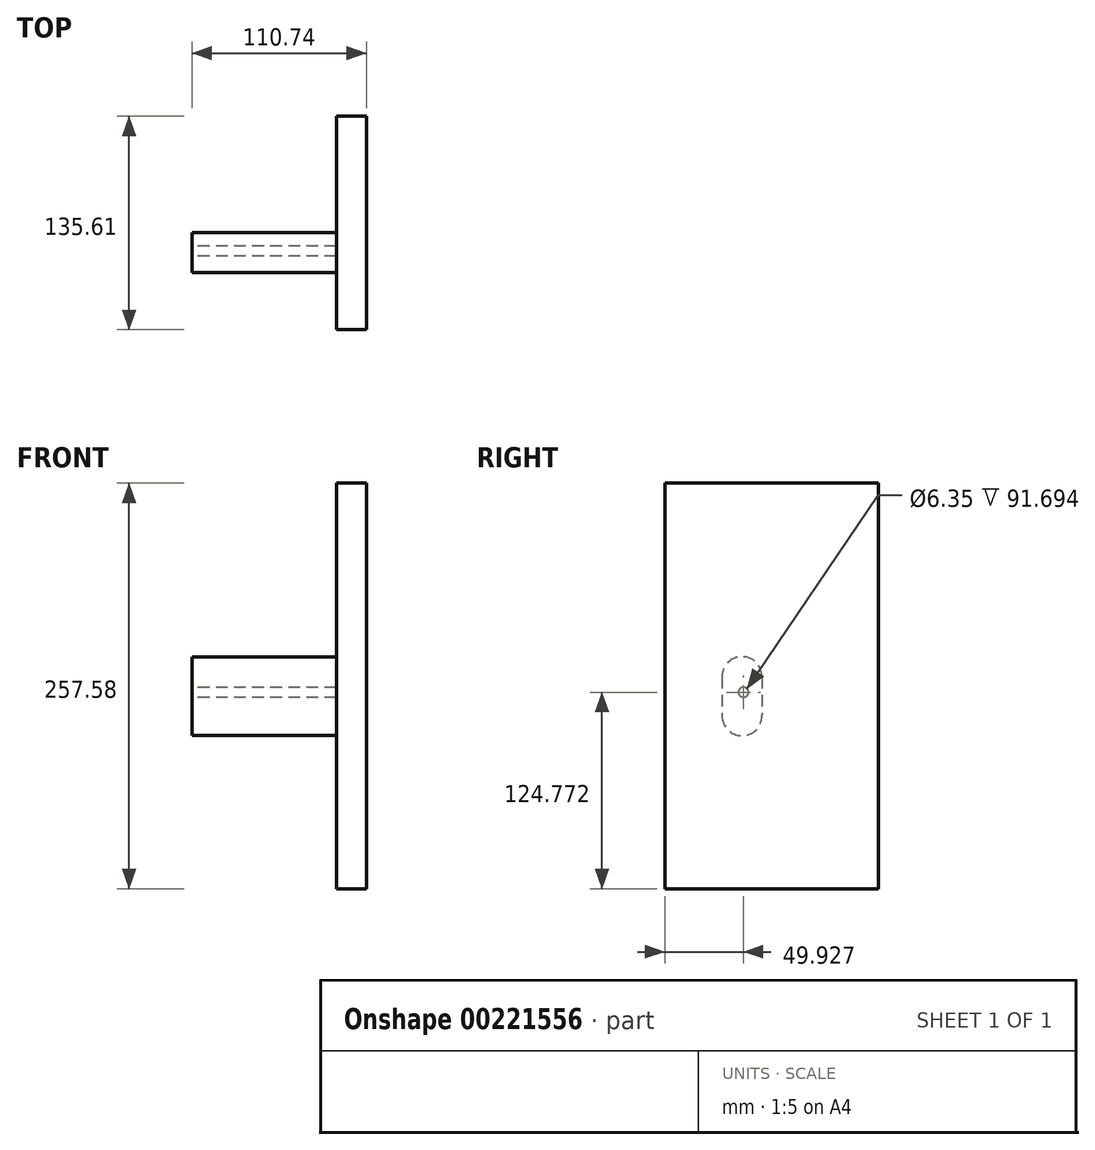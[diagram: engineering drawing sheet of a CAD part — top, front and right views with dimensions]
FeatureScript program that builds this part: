
annotation { "Feature Type Name" : "Feature", "Feature Type Description" : "" }
export const myFeature = defineFeature(function(context is Context, id is Id, definition is map)
    precondition{}
    {
        {
            var Q0;
            Q0=qCreatedBy(makeId("Front.planeOp"),FACE);
            var sketch = newSketch(context, id + "F0", { "sketchPlane" : qUnion([Q0])});
            skLineSegment(sketch, "E0.bottom", {"start": v(-66.96, 56.83) * mm, "end": v(24.73, 56.83) * mm});
            skLineSegment(sketch, "E0.top", {"start": v(-66.96, 6.69) * mm, "end": v(24.73, 6.69) * mm});
            skLineSegment(sketch, "E0.left", {"start": v(-66.96, 56.83) * mm, "end": v(-66.96, 6.69) * mm});
            skLineSegment(sketch, "E0.right", {"start": v(24.73, 56.83) * mm, "end": v(24.73, 6.69) * mm});
            skSolve(sketch);
        }
        {
            var Q0;
            Q0 = qSketchRegion(id + "F0", true);
            extrude(context, id + "F1", {"entities" : qUnion([Q0]), "depth" : 25.4 * mm});
        }
        {
            var Q0;
            Q0=makeQuery(id+"F1.opExtrude","CAP_EDGE",EDGE,{"disambiguationData":[OSD([sQuery(id+"F0.wireOp",EDGE,"E0.bottom")])],"isStart":false});
            var Q1;
            Q1=makeQuery(id+"F1.opExtrude","CAP_EDGE",EDGE,{"disambiguationData":[OSD([sQuery(id+"F0.wireOp",EDGE,"E0.top")])],"isStart":false});
            var Q2;
            Q2=makeQuery(id+"F1.opExtrude","CAP_EDGE",EDGE,{"disambiguationData":[OSD([sQuery(id+"F0.wireOp",EDGE,"E0.bottom")])],"isStart":true});
            var Q3;
            Q3=makeQuery(id+"F1.opExtrude","CAP_EDGE",EDGE,{"disambiguationData":[OSD([sQuery(id+"F0.wireOp",EDGE,"E0.top")])],"isStart":true});
            fillet(context, id + "F2", {"entities" : qUnion([Q0, Q1, Q2, Q3]), "radius" : 12.7 * mm, "tangentPropagation" : true, "allowEdgeOverflow" : false});
        }
        {
            var Q0;
            Q0=makeQuery(id+"F1.opExtrude","SWEPT_FACE",FACE,{"disambiguationData":[OSD([sQuery(id+"F0.wireOp",EDGE,"E0.right")])]});
            var sketch = newSketch(context, id + "F3", { "sketchPlane" : qUnion([Q0])});
            skPoint(sketch, "E1", {"position": v(-11.82, 34.24) * mm});
            skSolve(sketch);
        }
        {
            var Q0;
            Q0=sQuery(id+"F3.wireOp",VERTEX,"E1");
            var Q1;
            Q1=makeQuery(id+"F1.opExtrude","SWEPT_BODY",BODY,{"disambiguationData":[OSD([sQuery(id+"F0.wireOp",EDGE,"E0.bottom"),sQuery(id+"F0.wireOp",EDGE,"E0.top"),sQuery(id+"F0.wireOp",EDGE,"E0.left"),sQuery(id+"F0.wireOp",EDGE,"E0.right")])]});
            hole(context, id + "F4", {"style" : HoleStyle.SIMPLE, "endStyle" : HoleEndStyle.THROUGH, "holeDiameter" : 6.35 * mm, "tappedDepth" : 12.7 * mm, "tapClearance" : 3, "locations" : qUnion([Q0]), "scope" : qUnion([Q1])});
        }
        {
            var Q0;
            Q0=makeQuery(id+"F1.opExtrude","SWEPT_FACE",FACE,{"disambiguationData":[OSD([sQuery(id+"F0.wireOp",EDGE,"E0.right")])]});
            var sketch = newSketch(context, id + "F5", { "sketchPlane" : qUnion([Q0])});
            skLineSegment(sketch, "E2.bottom", {"start": v(-61.75, 167.05) * mm, "end": v(73.86, 167.05) * mm});
            skLineSegment(sketch, "E2.top", {"start": v(-61.75, -90.53) * mm, "end": v(73.86, -90.53) * mm});
            skLineSegment(sketch, "E2.left", {"start": v(-61.75, 167.05) * mm, "end": v(-61.75, -90.53) * mm});
            skLineSegment(sketch, "E2.right", {"start": v(73.86, 167.05) * mm, "end": v(73.86, -90.53) * mm});
            skSolve(sketch);
        }
        {
            var Q0;
            Q0 = qSketchRegion(id + "F5", true);
            extrude(context, id + "F6", {"entities" : qUnion([Q0]), "operationType" : NewBodyOperationType.ADD, "depth" : 19.05 * mm});
        }
    });
